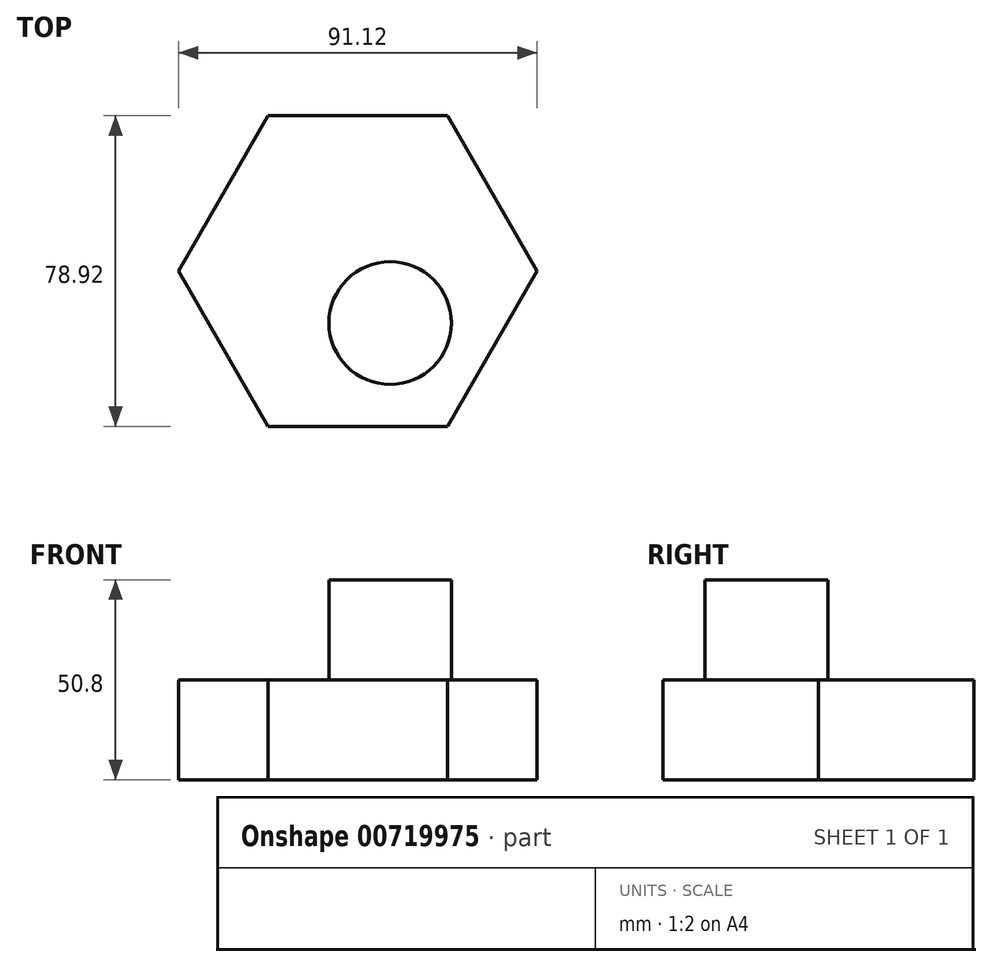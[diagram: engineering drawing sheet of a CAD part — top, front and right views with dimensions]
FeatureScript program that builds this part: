
annotation { "Feature Type Name" : "Feature", "Feature Type Description" : "" }
export const myFeature = defineFeature(function(context is Context, id is Id, definition is map)
    precondition{}
    {
        {
            var Q0;
            Q0=qCreatedBy(makeId("Top.planeOp"),FACE);
            var sketch = newSketch(context, id + "F0", { "sketchPlane" : qUnion([Q0])});
            skCircle(sketch, "E0.cCircle", {"center": v(0, 0) * mm, "radius": 39.46 * mm, "construction": true});
            skLineSegment(sketch, "E0.0", {"start": v(-22.78, 39.46) * mm, "end": v(22.78, 39.46) * mm});
            skLineSegment(sketch, "E0.1", {"start": v(22.78, 39.46) * mm, "end": v(45.56, 0) * mm});
            skLineSegment(sketch, "E0.2", {"start": v(45.56, 0) * mm, "end": v(22.78, -39.46) * mm});
            skLineSegment(sketch, "E0.3", {"start": v(22.78, -39.46) * mm, "end": v(-22.78, -39.46) * mm});
            skLineSegment(sketch, "E0.4", {"start": v(-22.78, -39.46) * mm, "end": v(-45.56, 0) * mm});
            skLineSegment(sketch, "E0.5", {"start": v(-45.56, 0) * mm, "end": v(-22.78, 39.46) * mm});
            skPoint(sketch, "E0.0.midPoint", {"position": v(0, 39.46) * mm});
            skSolve(sketch);
        }
        {
            var Q0;
            Q0=makeQuery(id+"F0.imprint","IMPRINT",FACE,{"disambiguationData":[TD([[makeQuery(id+"F0.imprint","IMPRINT",EDGE,{"derivedFrom":sQuery(id+"F0.wireOp",EDGE,"E0.0")}),-1.0]])]});
            extrude(context, id + "F1", {"entities" : qUnion([Q0]), "depth" : 25.4 * mm, "offsetDistance" : 25.4 * mm});
        }
        {
            var Q0;
            Q0=makeQuery(id+"F1.opExtrude","CAP_FACE",FACE,{"disambiguationData":[OSD([sQuery(id+"F0.wireOp",EDGE,"E0.0"),sQuery(id+"F0.wireOp",EDGE,"E0.1"),sQuery(id+"F0.wireOp",EDGE,"E0.2"),sQuery(id+"F0.wireOp",EDGE,"E0.3"),sQuery(id+"F0.wireOp",EDGE,"E0.4"),sQuery(id+"F0.wireOp",EDGE,"E0.5")])],"isStart":false});
            var sketch = newSketch(context, id + "F2", { "sketchPlane" : qUnion([Q0])});
            skCircle(sketch, "E1", {"center": v(8.23, -13.21) * mm, "radius": 15.57 * mm});
            skSolve(sketch);
        }
        {
            var Q0;
            Q0=makeQuery(id+"F2.imprint","IMPRINT",FACE,{"disambiguationData":[TD([[makeQuery(id+"F2.imprint","IMPRINT",EDGE,{"derivedFrom":sQuery(id+"F2.wireOp",EDGE,"E1")}),1.0]])]});
            extrude(context, id + "F3", {"entities" : qUnion([Q0]), "operationType" : NewBodyOperationType.ADD, "depth" : 25.4 * mm, "offsetDistance" : 25.4 * mm});
        }
    });
